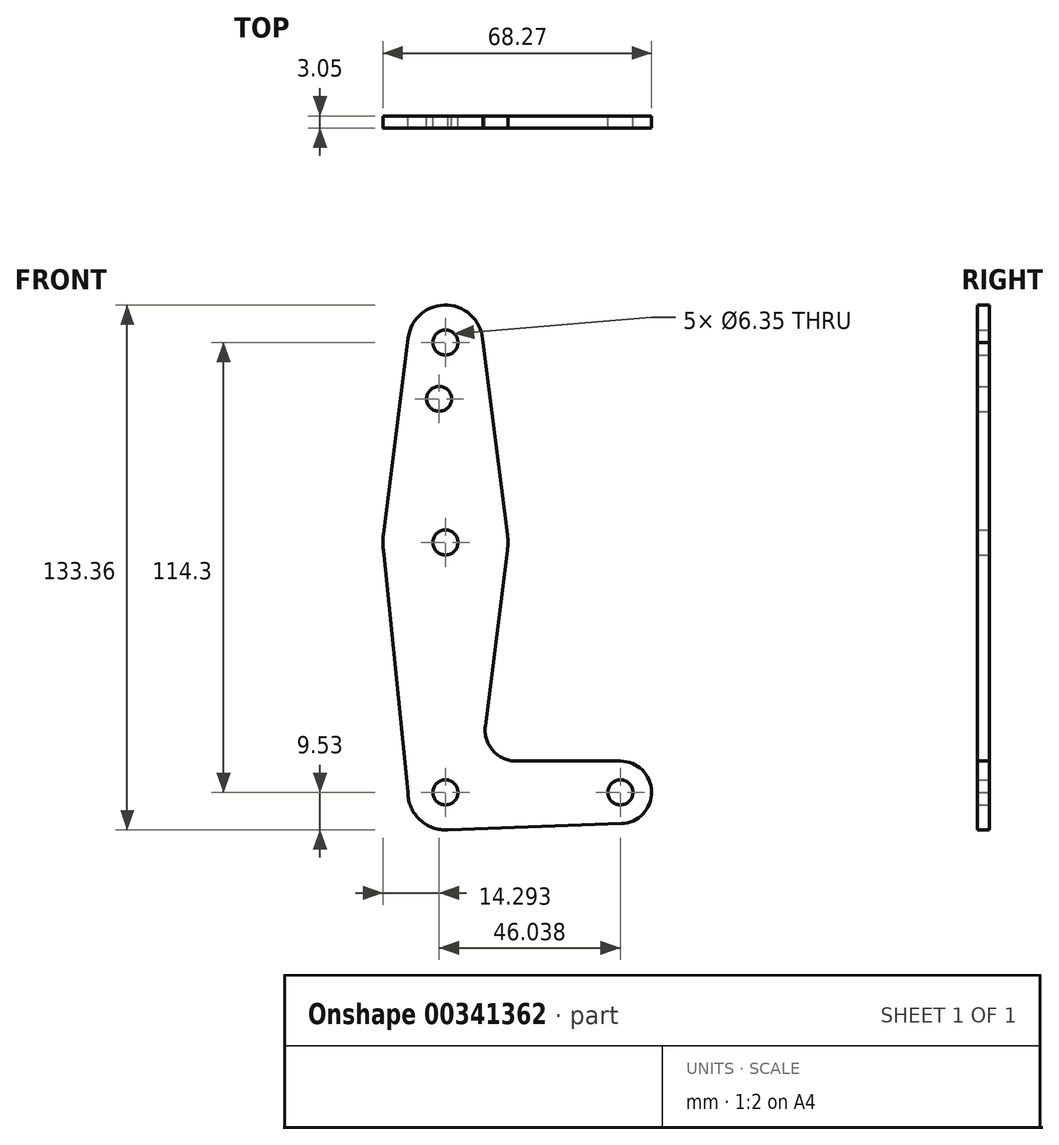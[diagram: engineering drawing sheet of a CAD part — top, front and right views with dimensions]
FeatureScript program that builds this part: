
annotation { "Feature Type Name" : "Feature", "Feature Type Description" : "" }
export const myFeature = defineFeature(function(context is Context, id is Id, definition is map)
    precondition{}
    {
        {
            var Q0;
            Q0=qCreatedBy(makeId("Front.planeOp"),FACE);
            var sketch = newSketch(context, id + "F0", { "sketchPlane" : qUnion([Q0])});
            skLineSegment(sketch, "E0", {"start": v(0, 0) * mm, "end": v(0, 114.3) * mm, "construction": true});
            skLineSegment(sketch, "E1", {"start": v(0, 0) * mm, "end": v(44.45, 0) * mm, "construction": true});
            skCircle(sketch, "E2", {"center": v(0, 63.5) * mm, "radius": 15.88 * mm});
            skCircle(sketch, "E3", {"center": v(0, 114.3) * mm, "radius": 9.53 * mm});
            skCircle(sketch, "E4", {"center": v(0, 0) * mm, "radius": 9.53 * mm});
            skCircle(sketch, "E5", {"center": v(44.45, 0) * mm, "radius": 7.94 * mm});
            skLineSegment(sketch, "E6", {"start": v(-9.45, 115.5) * mm, "end": v(-15.75, 65.48) * mm});
            skLineSegment(sketch, "E7", {"start": v(9.52, 114.3) * mm, "end": v(15.75, 65.48) * mm});
            skLineSegment(sketch, "E8", {"start": v(15.75, 61.52) * mm, "end": v(10.13, 16.88) * mm});
            skLineSegment(sketch, "E9", {"start": v(-15.88, 63.5) * mm, "end": v(-9.52, 0) * mm});
            skLineSegment(sketch, "E10", {"start": v(18.01, 7.94) * mm, "end": v(44.45, 7.94) * mm});
            skLineSegment(sketch, "E11", {"start": v(0, -9.53) * mm, "end": v(44.73, -7.93) * mm});
            skCircle(sketch, "E12", {"center": v(0, 114.3) * mm, "radius": 3.18 * mm});
            skCircle(sketch, "E13", {"center": v(0, 63.5) * mm, "radius": 3.18 * mm});
            skCircle(sketch, "E14", {"center": v(0, 0) * mm, "radius": 3.18 * mm});
            skCircle(sketch, "E15", {"center": v(44.45, 0) * mm, "radius": 3.18 * mm});
            skCircle(sketch, "E16", {"center": v(-1.59, 100) * mm, "radius": 3.18 * mm});
            skArc(sketch, "E17.filletArc", {"start": v(10.13, 16.88) * mm, "mid": v(12.05, 10.63) * mm, "end": v(18.01, 7.94) * mm});
            skSolve(sketch);
        }
        {
            var Q0;
            Q0 = qSketchRegion(id + "F0", true);
            extrude(context, id + "F1", {"entities" : qUnion([Q0]), "depth" : 3.05 * mm});
        }
    });
